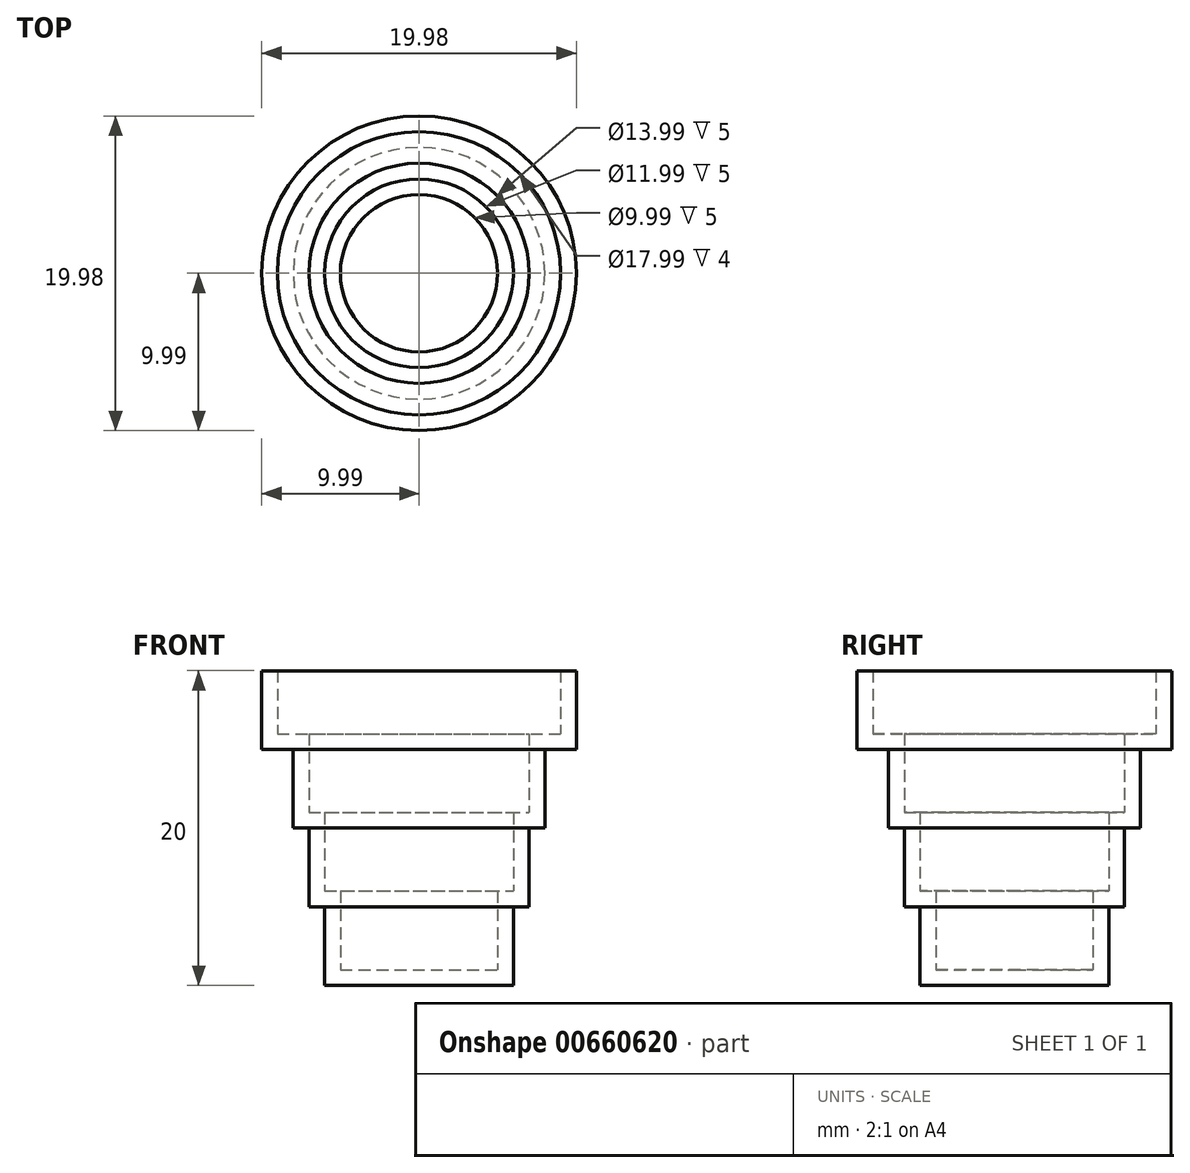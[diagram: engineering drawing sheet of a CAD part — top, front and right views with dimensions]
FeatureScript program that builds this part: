
annotation { "Feature Type Name" : "Feature", "Feature Type Description" : "" }
export const myFeature = defineFeature(function(context is Context, id is Id, definition is map)
    precondition{}
    {
        {
            var Q0;
            Q0=qCreatedBy(makeId("Front.planeOp"),FACE);
            var sketch = newSketch(context, id + "F0", { "sketchPlane" : qUnion([Q0])});
            skLineSegment(sketch, "E0", {"start": v(-9, 23.87) * mm, "end": v(-10, 23.87) * mm});
            skLineSegment(sketch, "E1", {"start": v(-10, 23.87) * mm, "end": v(-10, 18.87) * mm});
            skLineSegment(sketch, "E2", {"start": v(-10, 18.87) * mm, "end": v(-8, 18.87) * mm});
            skLineSegment(sketch, "E3", {"start": v(-8, 18.87) * mm, "end": v(-8, 13.87) * mm});
            skLineSegment(sketch, "E4", {"start": v(-8, 13.87) * mm, "end": v(-7, 13.87) * mm});
            skLineSegment(sketch, "E5", {"start": v(-7, 13.87) * mm, "end": v(-7, 8.87) * mm});
            skLineSegment(sketch, "E6", {"start": v(-7, 8.87) * mm, "end": v(-6, 8.87) * mm});
            skLineSegment(sketch, "E7", {"start": v(-6, 8.87) * mm, "end": v(-6, 3.87) * mm});
            skLineSegment(sketch, "E8", {"start": v(-6, 3.87) * mm, "end": v(0, 3.87) * mm});
            skLineSegment(sketch, "E9", {"start": v(0, 46.63) * mm, "end": v(0, -21.95) * mm, "construction": true});
            skLineSegment(sketch, "E10", {"start": v(-9, 23.87) * mm, "end": v(-9, 19.87) * mm});
            skLineSegment(sketch, "E11", {"start": v(-9, 19.87) * mm, "end": v(-7, 19.87) * mm});
            skLineSegment(sketch, "E12", {"start": v(-7, 19.87) * mm, "end": v(-7, 14.87) * mm});
            skLineSegment(sketch, "E13", {"start": v(-7, 14.87) * mm, "end": v(-6, 14.87) * mm});
            skLineSegment(sketch, "E14", {"start": v(-6, 14.87) * mm, "end": v(-6, 9.87) * mm});
            skLineSegment(sketch, "E15", {"start": v(-6, 9.87) * mm, "end": v(-5, 9.87) * mm});
            skLineSegment(sketch, "E16", {"start": v(-5, 9.87) * mm, "end": v(-5, 4.87) * mm});
            skLineSegment(sketch, "E17", {"start": v(-5, 4.87) * mm, "end": v(0, 4.87) * mm});
            skPoint(sketch, "E18.orphan", {"position": v(0, 23.87) * mm});
            skSolve(sketch);
        }
        {
            var Q0;
            Q0=sQuery(id+"F0.wireOp",EDGE,"E1");
            var Q1;
            Q1=sQuery(id+"F0.wireOp",EDGE,"E16");
            var Q2;
            Q2=sQuery(id+"F0.wireOp",EDGE,"E11");
            var Q3;
            Q3=sQuery(id+"F0.wireOp",EDGE,"E2");
            var Q4;
            Q4=sQuery(id+"F0.wireOp",EDGE,"E5");
            var Q5;
            Q5=sQuery(id+"F0.wireOp",EDGE,"E3");
            var Q6;
            Q6=sQuery(id+"F0.wireOp",EDGE,"E7");
            var Q7;
            Q7=sQuery(id+"F0.wireOp",EDGE,"E4");
            var Q8;
            Q8=sQuery(id+"F0.wireOp",EDGE,"E6");
            var Q9;
            Q9=sQuery(id+"F0.wireOp",EDGE,"E13");
            var Q10;
            Q10=sQuery(id+"F0.wireOp",EDGE,"E10");
            var Q11;
            Q11=sQuery(id+"F0.wireOp",EDGE,"E14");
            var Q12;
            Q12=sQuery(id+"F0.wireOp",EDGE,"E15");
            var Q13;
            Q13=sQuery(id+"F0.wireOp",EDGE,"E0");
            var Q14;
            Q14=sQuery(id+"F0.wireOp",EDGE,"E12");
            var Q15;
            Q15=sQuery(id+"F0.wireOp",EDGE,"E8");
            var Q16;
            Q16=sQuery(id+"F0.wireOp",EDGE,"E17");
            var Q17;
            Q17=sQuery(id+"F0.wireOp",EDGE,"E9");
            revolve(context, id + "F1", {"bodyType" : ToolBodyType.SURFACE, "surfaceEntities" : qUnion([Q0, Q1, Q2, Q3, Q4, Q5, Q6, Q7, Q8, Q9, Q10, Q11, Q12, Q13, Q14, Q15, Q16]), "axis" : qUnion([Q17]), "revolveType" : RevolveType.FULL});
        }
    });
